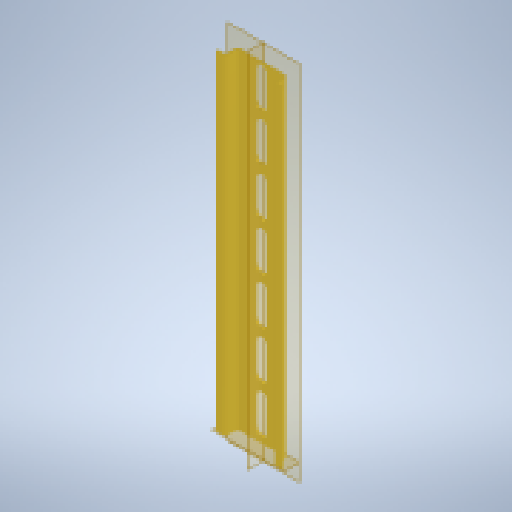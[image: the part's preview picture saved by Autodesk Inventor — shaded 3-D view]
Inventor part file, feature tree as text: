
AUTODESK INVENTOR PART (.ipt)
format: ipt  version: 2025.2 (Build 292293000, 293)  size: 190,464 bytes
history: native  units: mm
features: extrude x2, sketch x2, pattern_linear x1
ambient origin geometry x8: Origin, YZ Plane, XZ Plane, XY Plane, X Axis, Y Axis, Z Axis, Center Point
bodies: Solid1 (feature_tree)
feature tree (5):
  extrude  "Extrusion1"  Depth=175.0mm TaperAngle=0.0deg
  extrude  "Extrusion2"  Depth=3.0mm
  pattern_linear  "Rectangular Pattern1"  [2 undecoded]
  sketch  "Sketch_2"  dims[d0=175.0mm d1=0.0mm d2=2.0mm d3=0.0mm]
  sketch  "Sketch_6"  dims[d4=800.0mm d6=25.0mm d7=10.0mm d9=0.0mm d13=3.0mm]
note: 2 required parameter values undecoded (feature->parameter linkage not recoverable at this tier; creation-order binding heuristic only, values carry confidence <= 0.55)
